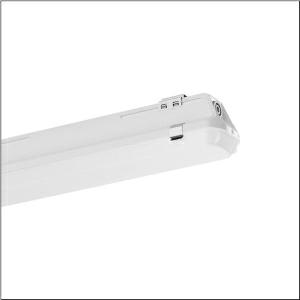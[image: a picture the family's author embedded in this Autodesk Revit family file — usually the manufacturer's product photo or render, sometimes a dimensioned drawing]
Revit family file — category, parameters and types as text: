
# Revit family: monsun_r__11_51fp207p460h_8ebd
name_source: partatom
category: Lighting Fixtures
units: mm (PartAtom-declared; Revit-internal decimal feet)

## family parameters
Cut with Voids When Loaded = No
Host = Face
Light Source = No
Part Type = Normal
Room Calculation Point = No
Round Connector Dimension = Use Diameter
Shared = No

## types (1)
- Monsun® 11 (1 x LED, 6030 lm, 37.7 W, 4000K)
    Apparent Load = 38 VA
    CIE Flux Codes = 45 75 93 94 100
    Color Rendering = 80
    Color Temperature = 4000K
    Default Elevation = 1800 mm
    Description = Monsun® 11, damp-proof luminaire, chain hanger, primary optical cover: enclosure, of PC, light emission: direct distribution, primary light characteristic: symmetric, installation type: suspended mounting, surface-mounted, horizontal mounting, vertical mounting, LED, rated luminous flux: 6.030lm, luminous efficacy: 160lm/W, light colour: 840, colour temperature: 4000K, control gear: ECG, with terminal, 3-pole, max. 2.5mm², mains connection: 220..240V, AC, 50/60Hz, rated input power: 38W, luminaire housing, of glass-fibre reinforced polyester, uncoated, bright grey, incl. chain hanger, length: 1.590mm, width: 90mm, height: 88mm, clip for enclosure, of stainless steel (V2A), ceiling mounting element, of stainless steel (V2A), chain hanger, of stainless steel (V2A), protection rating (complete): IP66, insulation class (complete): insulation class I (protective earthing), certification: CE, ENEC, VDE, UKCA, protection symbol: D, impact resistance: IK08, permissible operating ambient temperature: -35..+40°C, standard: EN 50419, EN 60598-2-1, no direct snow, no direct sun, no direct rain, for indoor or canopied outdoor use, corresponds to IFS (International Featured Standards) requirements for safety and quality in the food industry, contact your sales advisor before using the luminaires in applications with unclear chemical exposure, large temperature fluctuations or condensation-forming humidity, LABS conformity tested according to VDMA 24364:2018-05, packaging unit: 1 piece
    Height = 89 mm
    Lamp = 1 x LED
    Lamp Light Flux = 6030 lm
    Lamp Power = 37.7 W
    Lamp count = 1
    Length = 1590 mm
    Luminous efficacy = 160 lm/W
    Manufacturer = Siteco
    ModVariant = No
    Model = 51FP207P460H
    Mounting Place = Ceiling
    Mounting Type = Surface mounted
    Number of Poles = 1
    OnlyDefault = Yes
    Power Factor = 1
    Product Name = Monsun® 11
    Product group = damp-proof luminaire
    ProductGroupID = 301
    Protection Class = Protection class I
    Protection Degree = IP 66
    RLX_Detail_Level = 1
    RLX_Emergency_Light_Flux = 0 lm
    RLX_Emergency_Type = 0
    RLX_Emergency_Type_DB = No
    RlxData = <blob elided: 88549 chars, md5=c50a42c0>
    Socket = socket
    Standby Power = 0 W
    System Light Flux = 6030 lm
    System Power = 38 W
    Type Comments = Product without accessories
    Type Image = l_1004748.jpg
    URL = http://relux.com
    VarID = ---
    Voltage = 0 V
    Weight = 0.00 kg
    Width = 90 mm

## geometry (parser evidence)
native form markers: Blend x4, Sweep x15
no freeform markers — native parametric forms only
